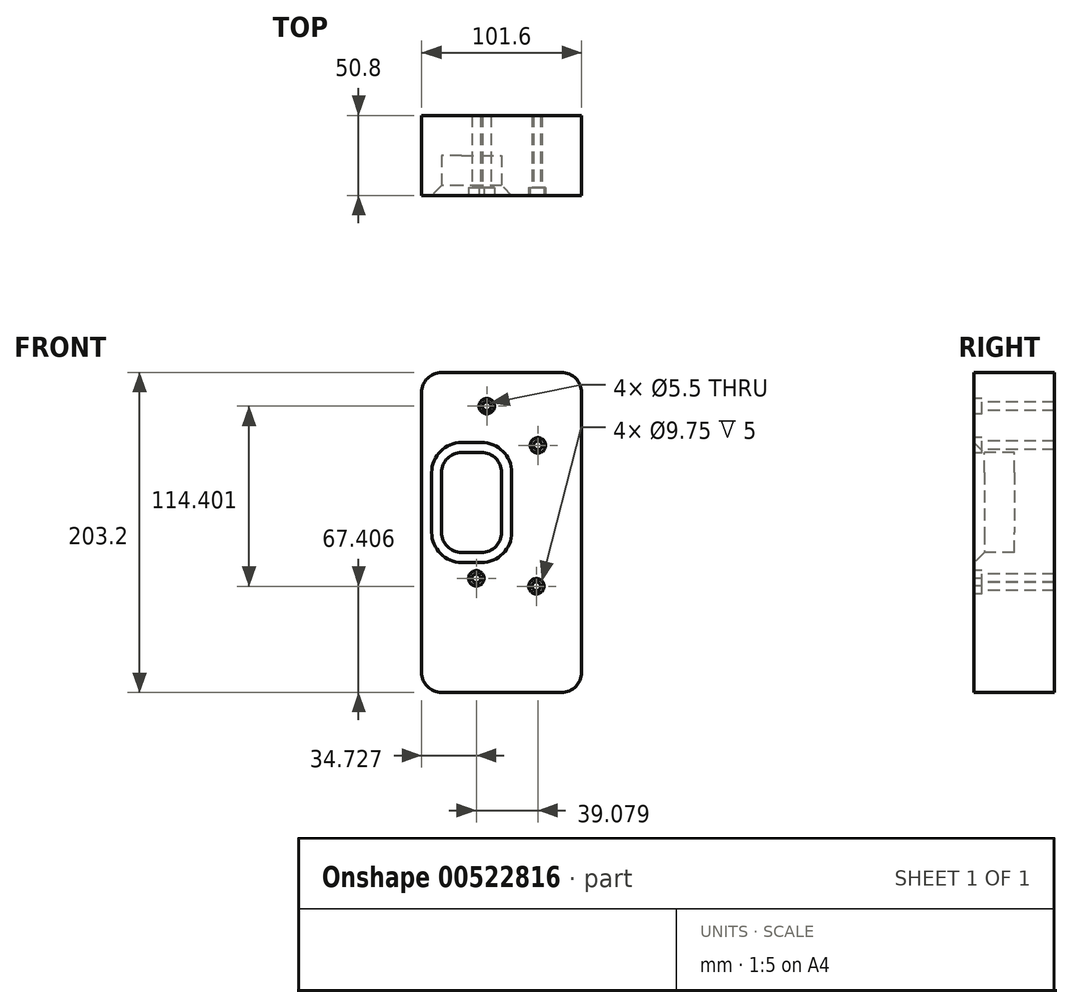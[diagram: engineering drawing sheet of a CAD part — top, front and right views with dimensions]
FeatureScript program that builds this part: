
annotation { "Feature Type Name" : "Feature", "Feature Type Description" : "" }
export const myFeature = defineFeature(function(context is Context, id is Id, definition is map)
    precondition{}
    {
        {
            var Q0;
            Q0=qCreatedBy(makeId("Top.planeOp"),FACE);
            var sketch = newSketch(context, id + "F0", { "sketchPlane" : qUnion([Q0])});
            skLineSegment(sketch, "E0.bottom", {"start": v(-50.8, 25.4) * mm, "end": v(50.8, 25.4) * mm});
            skLineSegment(sketch, "E0.top", {"start": v(-50.8, -25.4) * mm, "end": v(50.8, -25.4) * mm});
            skLineSegment(sketch, "E0.left", {"start": v(-50.8, 25.4) * mm, "end": v(-50.8, -25.4) * mm});
            skLineSegment(sketch, "E0.right", {"start": v(50.8, 25.4) * mm, "end": v(50.8, -25.4) * mm});
            skLineSegment(sketch, "E1", {"start": v(-50.8, 25.4) * mm, "end": v(50.8, -25.4) * mm, "construction": true});
            skSolve(sketch);
        }
        {
            var Q0;
            Q0 = qSketchRegion(id + "F0", true);
            extrude(context, id + "F1", {"entities" : qUnion([Q0]), "endBound" : BoundingType.SYMMETRIC, "depth" : 203.2 * mm, "offsetDistance" : 25.4 * mm});
        }
        {
            var Q0;
            Q0=makeQuery(id+"F1.opExtrude","SWEPT_FACE",FACE,{"disambiguationData":[OSD([sQuery(id+"F0.wireOp",EDGE,"E0.top")])]});
            var sketch = newSketch(context, id + "F2", { "sketchPlane" : qUnion([Q0])});
            skPoint(sketch, "E2", {"position": v(-9.45, 80.2) * mm});
            skPoint(sketch, "E3", {"position": v(23, 55.3) * mm});
            skPoint(sketch, "E4", {"position": v(-16.07, -29.15) * mm});
            skPoint(sketch, "E5", {"position": v(22.06, -34.2) * mm});
            skSolve(sketch);
        }
        {
            var Q0;
            Q0=sQuery(id+"F2.wireOp",VERTEX,"E2");
            var Q1;
            Q1=sQuery(id+"F2.wireOp",VERTEX,"E3");
            var Q2;
            Q2=sQuery(id+"F2.wireOp",VERTEX,"E4");
            var Q3;
            Q3=sQuery(id+"F2.wireOp",VERTEX,"E5");
            var Q4;
            Q4=makeQuery(id+"F1.opExtrude","SWEPT_BODY",BODY,{"disambiguationData":[OSD([sQuery(id+"F0.wireOp",EDGE,"E0.bottom"),sQuery(id+"F0.wireOp",EDGE,"E0.top"),sQuery(id+"F0.wireOp",EDGE,"E0.left"),sQuery(id+"F0.wireOp",EDGE,"E0.right")])]});
            hole(context, id + "F3", {"style" : HoleStyle.C_BORE, "endStyle" : HoleEndStyle.THROUGH, "standardTappedOrClearance" : lookupTablePath({ "standard" : "ISO", "fit" : "Normal", "size" : "M5", "type" : "Clearance" }), "standardBlindInLast" : lookupTablePath({ "fit" : "Standard", "standard" : "ISO", "size" : "M5", "type" : "Clearance" }), "holeDiameter" : 5.5 * mm, "cBoreDiameter" : 9.75 * mm, "cBoreDepth" : 5 * mm, "isTappedThrough" : true, "tappedDepth" : 12.7 * mm, "tapClearance" : 3, "locations" : qUnion([Q0, Q1, Q2, Q3]), "scope" : qUnion([Q4])});
        }
        {
            var Q0;
            Q0=makeQuery(id+"F1.opExtrude","CAP_EDGE",EDGE,{"disambiguationData":[OSD([sQuery(id+"F0.wireOp",EDGE,"E0.left")])],"isStart":false});
            var Q1;
            Q1=makeQuery(id+"F1.opExtrude","CAP_EDGE",EDGE,{"disambiguationData":[OSD([sQuery(id+"F0.wireOp",EDGE,"E0.right")])],"isStart":false});
            var Q2;
            Q2=makeQuery(id+"F1.opExtrude","CAP_EDGE",EDGE,{"disambiguationData":[OSD([sQuery(id+"F0.wireOp",EDGE,"E0.left")])],"isStart":true});
            var Q3;
            Q3=makeQuery(id+"F1.opExtrude","CAP_EDGE",EDGE,{"disambiguationData":[OSD([sQuery(id+"F0.wireOp",EDGE,"E0.right")])],"isStart":true});
            fillet(context, id + "F4", {"entities" : qUnion([Q0, Q1, Q2, Q3]), "radius" : 12.7 * mm, "tangentPropagation" : true, "allowEdgeOverflow" : false});
        }
        {
            var Q0;
            Q0=makeQuery(id+"F1.opExtrude","SWEPT_FACE",FACE,{"disambiguationData":[OSD([sQuery(id+"F0.wireOp",EDGE,"E0.top")])]});
            var sketch = newSketch(context, id + "F5", { "sketchPlane" : qUnion([Q0])});
            skLineSegment(sketch, "E6.bottom", {"start": v(-38.1, 50.8) * mm, "end": v(0, 50.8) * mm});
            skLineSegment(sketch, "E6.top", {"start": v(-38.1, -12.7) * mm, "end": v(0, -12.7) * mm});
            skLineSegment(sketch, "E6.left", {"start": v(-38.1, 50.8) * mm, "end": v(-38.1, -12.7) * mm});
            skLineSegment(sketch, "E6.right", {"start": v(0, 50.8) * mm, "end": v(0, -12.7) * mm});
            skSolve(sketch);
        }
        {
            var Q0;
            Q0 = qSketchRegion(id + "F5", true);
            extrude(context, id + "F6", {"entities" : qUnion([Q0]), "operationType" : NewBodyOperationType.REMOVE, "oppositeDirection" : true, "depth" : 25.4 * mm, "offsetDistance" : 25.4 * mm});
        }
        {
            var Q0;
            Q0=makeQuery(id+"F6.boolean.opBoolean","COPY",EDGE,{"derivedFrom":makeQuery(id+"F6.opExtrude","SWEPT_EDGE",EDGE,{"disambiguationData":[OSD([sQuery(id+"F5.wireOp",EDGE,"E6.bottom"),sQuery(id+"F5.wireOp",EDGE,"E6.right")])]})});
            var Q1;
            Q1=makeQuery(id+"F6.boolean.opBoolean","COPY",EDGE,{"derivedFrom":makeQuery(id+"F6.opExtrude","SWEPT_EDGE",EDGE,{"disambiguationData":[OSD([sQuery(id+"F5.wireOp",EDGE,"E6.bottom"),sQuery(id+"F5.wireOp",EDGE,"E6.left")])]})});
            var Q2;
            Q2=makeQuery(id+"F6.boolean.opBoolean","COPY",EDGE,{"derivedFrom":makeQuery(id+"F6.opExtrude","SWEPT_EDGE",EDGE,{"disambiguationData":[OSD([sQuery(id+"F5.wireOp",EDGE,"E6.top"),sQuery(id+"F5.wireOp",EDGE,"E6.left")])]})});
            var Q3;
            Q3=makeQuery(id+"F6.boolean.opBoolean","COPY",EDGE,{"derivedFrom":makeQuery(id+"F6.opExtrude","SWEPT_EDGE",EDGE,{"disambiguationData":[OSD([sQuery(id+"F5.wireOp",EDGE,"E6.top"),sQuery(id+"F5.wireOp",EDGE,"E6.right")])]})});
            fillet(context, id + "F7", {"entities" : qUnion([Q0, Q1, Q2, Q3]), "radius" : 12.7 * mm, "tangentPropagation" : true, "allowEdgeOverflow" : false});
        }
        {
            var Q0;
            Q0=makeQuery(id+"F7.opFillet","BLEND_EDGE",EDGE,{"blendedFrom":[makeQuery(id+"F6.boolean.opBoolean","COPY",EDGE,{"derivedFrom":makeQuery(id+"F6.opExtrude","SWEPT_EDGE",EDGE,{"disambiguationData":[OSD([sQuery(id+"F5.wireOp",EDGE,"E6.bottom"),sQuery(id+"F5.wireOp",EDGE,"E6.left")])]})}),makeQuery(id+"F1.opExtrude","SWEPT_FACE",FACE,{"disambiguationData":[OSD([sQuery(id+"F0.wireOp",EDGE,"E0.top")])]})],"blendedInto":[makeQuery(id+"F1.opExtrude","SWEPT_FACE",FACE,{"disambiguationData":[OSD([sQuery(id+"F0.wireOp",EDGE,"E0.top")])]})]});
            chamfer(context, id + "F8", {"entities" : qUnion([Q0]), "width" : 6.35 * mm, "tangentPropagation" : true});
        }
    });
